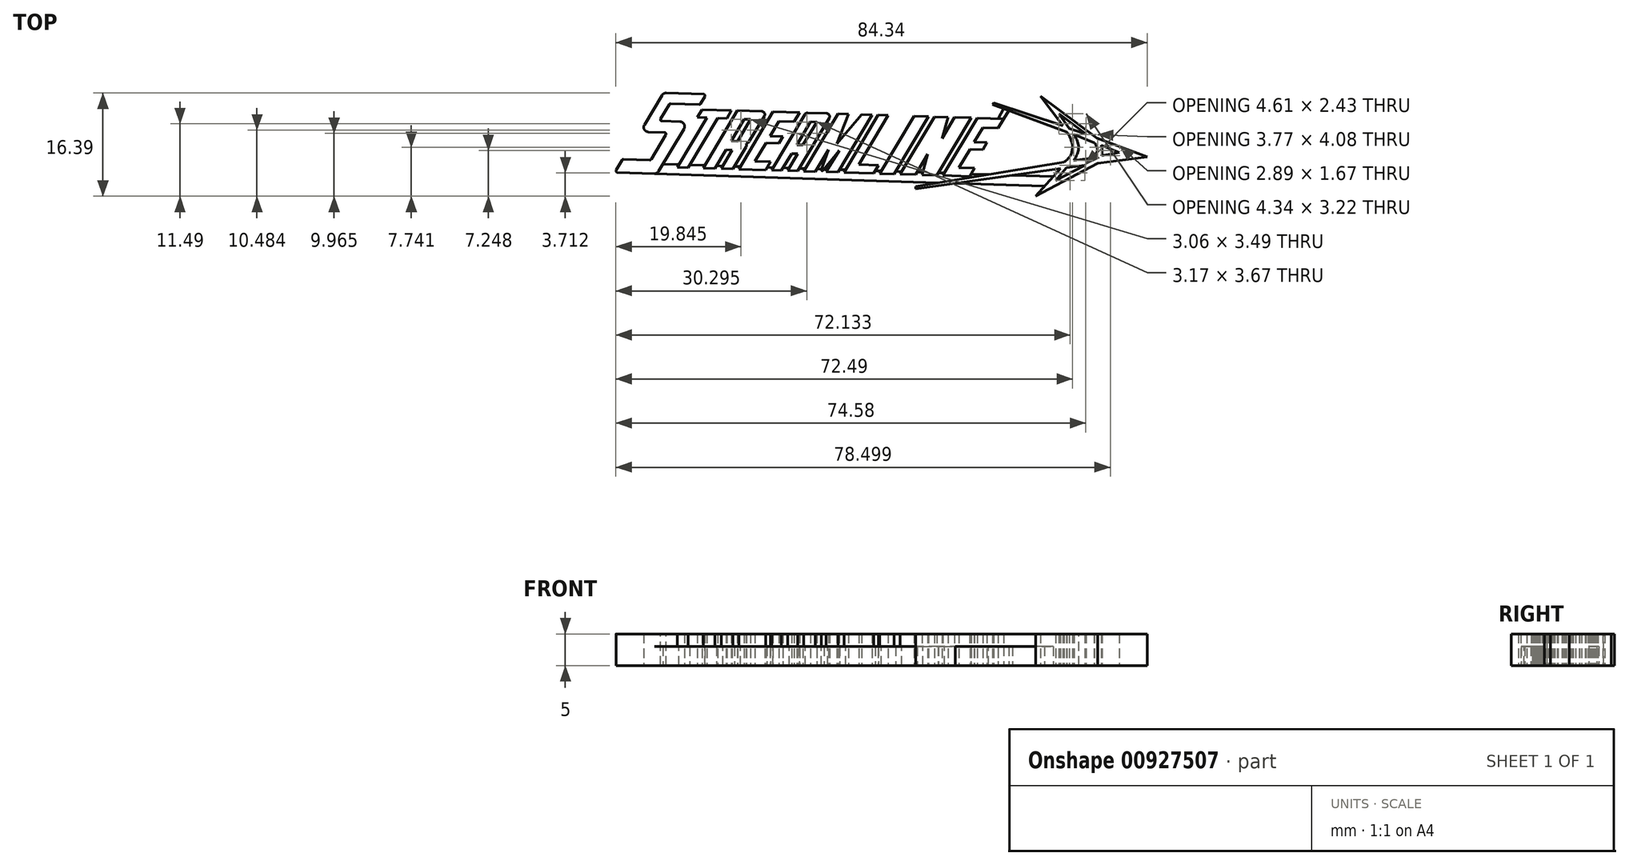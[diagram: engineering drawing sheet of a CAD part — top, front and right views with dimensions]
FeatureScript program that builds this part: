
annotation { "Feature Type Name" : "Feature", "Feature Type Description" : "" }
export const myFeature = defineFeature(function(context is Context, id is Id, definition is map)
    precondition{}
    {
        {
            var Q0;
            Q0=qCreatedBy(makeId("Top.planeOp"),FACE);
            var sketch = newSketch(context, id + "F0", { "sketchPlane" : qUnion([Q0])});
            skLineSegment(sketch, "E0", {"start": v(-39.16, -4.36) * mm, "end": v(-37.92, -2.27) * mm});
            skLineSegment(sketch, "E1", {"start": v(-37.92, -2.27) * mm, "end": v(-33.45, -2.42) * mm});
            skLineSegment(sketch, "E2", {"start": v(-33.45, -2.42) * mm, "end": v(-30.85, 1.96) * mm});
            skLineSegment(sketch, "E3", {"start": v(-30.85, 1.96) * mm, "end": v(-35.11, 2.1) * mm});
            skLineSegment(sketch, "E4", {"start": v(-35.11, 2.1) * mm, "end": v(-31.45, 8.25) * mm});
            skLineSegment(sketch, "E5", {"start": v(-31.45, 8.25) * mm, "end": v(-24.64, 8.03) * mm});
            skLineSegment(sketch, "E6", {"start": v(-24.64, 8.03) * mm, "end": v(-25.6, 6.4) * mm});
            skLineSegment(sketch, "E7", {"start": v(-25.6, 6.4) * mm, "end": v(-30.45, 6.55) * mm});
            skLineSegment(sketch, "E8", {"start": v(-30.45, 6.55) * mm, "end": v(-32.1, 3.8) * mm});
            skLineSegment(sketch, "E9", {"start": v(-32.1, 3.8) * mm, "end": v(-27.53, 3.65) * mm});
            skLineSegment(sketch, "E10", {"start": v(-27.53, 3.65) * mm, "end": v(-32.42, -4.57) * mm});
            skLineSegment(sketch, "E11", {"start": v(-32.42, -4.57) * mm, "end": v(-39.16, -4.36) * mm});
            skLineSegment(sketch, "E12", {"start": v(-29.24, -3.55) * mm, "end": v(-24.55, 4.32) * mm});
            skLineSegment(sketch, "E13", {"start": v(-24.55, 4.32) * mm, "end": v(-26.02, 4.37) * mm});
            skLineSegment(sketch, "E14", {"start": v(-26.02, 4.37) * mm, "end": v(-25.28, 5.61) * mm});
            skLineSegment(sketch, "E15", {"start": v(-25.28, 5.61) * mm, "end": v(-20.64, 5.47) * mm});
            skLineSegment(sketch, "E16", {"start": v(-20.64, 5.47) * mm, "end": v(-21.38, 4.22) * mm});
            skLineSegment(sketch, "E17", {"start": v(-21.38, 4.22) * mm, "end": v(-22.84, 4.27) * mm});
            skLineSegment(sketch, "E18", {"start": v(-22.84, 4.27) * mm, "end": v(-27.53, -3.6) * mm});
            skLineSegment(sketch, "E19", {"start": v(-27.53, -3.6) * mm, "end": v(-29.24, -3.55) * mm});
            skLineSegment(sketch, "E20", {"start": v(-25.11, -3.68) * mm, "end": v(-19.68, 5.44) * mm});
            skLineSegment(sketch, "E21", {"start": v(-19.68, 5.44) * mm, "end": v(-14.98, 5.3) * mm});
            skLineSegment(sketch, "E22", {"start": v(-14.98, 5.3) * mm, "end": v(-17.95, 0.3) * mm});
            skLineSegment(sketch, "E23", {"start": v(-17.95, 0.3) * mm, "end": v(-18.28, 0.22) * mm});
            skLineSegment(sketch, "E24", {"start": v(-18.28, 0.22) * mm, "end": v(-18.2, -0.1) * mm});
            skLineSegment(sketch, "E25", {"start": v(-18.2, -0.1) * mm, "end": v(-20.4, -3.82) * mm});
            skLineSegment(sketch, "E26", {"start": v(-20.4, -3.82) * mm, "end": v(-22.26, -3.77) * mm});
            skLineSegment(sketch, "E27", {"start": v(-22.26, -3.77) * mm, "end": v(-20.5, -0.81) * mm});
            skLineSegment(sketch, "E28", {"start": v(-20.5, -0.81) * mm, "end": v(-21.5, -0.78) * mm});
            skLineSegment(sketch, "E29", {"start": v(-21.5, -0.78) * mm, "end": v(-23.26, -3.74) * mm});
            skLineSegment(sketch, "E30", {"start": v(-23.26, -3.74) * mm, "end": v(-25.11, -3.68) * mm});
            skLineSegment(sketch, "E31", {"start": v(-20.67, 0.62) * mm, "end": v(-18.6, 4.08) * mm});
            skLineSegment(sketch, "E32", {"start": v(-18.6, 4.08) * mm, "end": v(-17.6, 4.05) * mm});
            skLineSegment(sketch, "E33", {"start": v(-17.6, 4.05) * mm, "end": v(-19.67, 0.59) * mm});
            skLineSegment(sketch, "E34", {"start": v(-19.67, 0.59) * mm, "end": v(-20.67, 0.62) * mm});
            skLineSegment(sketch, "E35", {"start": v(-19.45, -3.85) * mm, "end": v(-14.02, 5.26) * mm});
            skLineSegment(sketch, "E36", {"start": v(-14.02, 5.26) * mm, "end": v(-9.8, 5.13) * mm});
            skLineSegment(sketch, "E37", {"start": v(-9.8, 5.13) * mm, "end": v(-10.67, 3.67) * mm});
            skLineSegment(sketch, "E38", {"start": v(-10.67, 3.67) * mm, "end": v(-13.11, 3.74) * mm});
            skLineSegment(sketch, "E39", {"start": v(-13.11, 3.74) * mm, "end": v(-14.5, 1.42) * mm});
            skLineSegment(sketch, "E40", {"start": v(-14.5, 1.42) * mm, "end": v(-12.46, 1.36) * mm});
            skLineSegment(sketch, "E41", {"start": v(-12.46, 1.36) * mm, "end": v(-13.12, 0.24) * mm});
            skLineSegment(sketch, "E42", {"start": v(-13.12, 0.24) * mm, "end": v(-15.16, 0.3) * mm});
            skLineSegment(sketch, "E43", {"start": v(-15.16, 0.3) * mm, "end": v(-16.9, -2.6) * mm});
            skLineSegment(sketch, "E44", {"start": v(-16.9, -2.6) * mm, "end": v(-14.45, -2.68) * mm});
            skLineSegment(sketch, "E45", {"start": v(-14.45, -2.68) * mm, "end": v(-15.23, -3.98) * mm});
            skLineSegment(sketch, "E46", {"start": v(-15.23, -3.98) * mm, "end": v(-19.45, -3.85) * mm});
            skLineSegment(sketch, "E47", {"start": v(-14.28, -4.01) * mm, "end": v(-8.85, 5.1) * mm});
            skLineSegment(sketch, "E48", {"start": v(-8.85, 5.1) * mm, "end": v(-4.68, 4.97) * mm});
            skLineSegment(sketch, "E49", {"start": v(-4.68, 4.97) * mm, "end": v(-10.11, -4.14) * mm});
            skLineSegment(sketch, "E50", {"start": v(-10.11, -4.14) * mm, "end": v(-11.7, -4.1) * mm});
            skLineSegment(sketch, "E51", {"start": v(-11.7, -4.1) * mm, "end": v(-10.09, -1.4) * mm});
            skLineSegment(sketch, "E52", {"start": v(-10.09, -1.4) * mm, "end": v(-11.09, -1.37) * mm});
            skLineSegment(sketch, "E53", {"start": v(-11.09, -1.37) * mm, "end": v(-12.7, -4.06) * mm});
            skLineSegment(sketch, "E54", {"start": v(-12.7, -4.06) * mm, "end": v(-14.28, -4.01) * mm});
            skLineSegment(sketch, "E55", {"start": v(-9.27, -0.02) * mm, "end": v(-7.1, 3.62) * mm});
            skLineSegment(sketch, "E56", {"start": v(-7.1, 3.62) * mm, "end": v(-8.1, 3.65) * mm});
            skLineSegment(sketch, "E57", {"start": v(-8.1, 3.65) * mm, "end": v(-10.27, 0) * mm});
            skLineSegment(sketch, "E58", {"start": v(-10.27, 0) * mm, "end": v(-9.27, -0.02) * mm});
            skLineSegment(sketch, "E59", {"start": v(-9.16, -4.17) * mm, "end": v(-3.73, 4.94) * mm});
            skLineSegment(sketch, "E60", {"start": v(-3.73, 4.94) * mm, "end": v(-2.06, 4.9) * mm});
            skLineSegment(sketch, "E61", {"start": v(-2.06, 4.9) * mm, "end": v(-3.9, 0.18) * mm});
            skLineSegment(sketch, "E62", {"start": v(-3.9, 0.18) * mm, "end": v(0.04, 4.83) * mm});
            skLineSegment(sketch, "E63", {"start": v(0.04, 4.83) * mm, "end": v(1.7, 4.78) * mm});
            skLineSegment(sketch, "E64", {"start": v(1.7, 4.78) * mm, "end": v(-3.72, -4.34) * mm});
            skLineSegment(sketch, "E65", {"start": v(-3.72, -4.34) * mm, "end": v(-5.58, -4.28) * mm});
            skLineSegment(sketch, "E66", {"start": v(-5.58, -4.28) * mm, "end": v(-3.54, -0.86) * mm});
            skLineSegment(sketch, "E67", {"start": v(-3.54, -0.86) * mm, "end": v(-6.67, -4.75) * mm});
            skLineSegment(sketch, "E68", {"start": v(-6.67, -4.75) * mm, "end": v(-5.24, -0.77) * mm});
            skLineSegment(sketch, "E69", {"start": v(-5.24, -0.77) * mm, "end": v(-7.3, -4.23) * mm});
            skLineSegment(sketch, "E70", {"start": v(-7.3, -4.23) * mm, "end": v(-9.16, -4.17) * mm});
            skLineSegment(sketch, "E71", {"start": v(-2.77, -4.37) * mm, "end": v(2.66, 4.75) * mm});
            skLineSegment(sketch, "E72", {"start": v(2.66, 4.75) * mm, "end": v(4.24, 4.7) * mm});
            skLineSegment(sketch, "E73", {"start": v(4.24, 4.7) * mm, "end": v(-0.4, -3.11) * mm});
            skLineSegment(sketch, "E74", {"start": v(-0.4, -3.11) * mm, "end": v(2.74, -3.21) * mm});
            skLineSegment(sketch, "E75", {"start": v(2.74, -3.21) * mm, "end": v(1.96, -4.52) * mm});
            skLineSegment(sketch, "E76", {"start": v(1.96, -4.52) * mm, "end": v(-2.77, -4.37) * mm});
            skLineSegment(sketch, "E77", {"start": v(2.91, -4.55) * mm, "end": v(8.34, 4.57) * mm});
            skLineSegment(sketch, "E78", {"start": v(8.34, 4.57) * mm, "end": v(10.63, 4.5) * mm});
            skLineSegment(sketch, "E79", {"start": v(10.63, 4.5) * mm, "end": v(5.2, -4.62) * mm});
            skLineSegment(sketch, "E80", {"start": v(5.2, -4.62) * mm, "end": v(2.91, -4.55) * mm});
            skLineSegment(sketch, "E81", {"start": v(6.16, -4.65) * mm, "end": v(11.59, 4.47) * mm});
            skLineSegment(sketch, "E82", {"start": v(11.59, 4.47) * mm, "end": v(13.76, 4.4) * mm});
            skLineSegment(sketch, "E83", {"start": v(13.76, 4.4) * mm, "end": v(12.8, 1.04) * mm});
            skLineSegment(sketch, "E84", {"start": v(12.8, 1.04) * mm, "end": v(14.79, 4.37) * mm});
            skLineSegment(sketch, "E85", {"start": v(14.79, 4.37) * mm, "end": v(17.42, 4.29) * mm});
            skLineSegment(sketch, "E86", {"start": v(17.42, 4.29) * mm, "end": v(11.99, -4.83) * mm});
            skLineSegment(sketch, "E87", {"start": v(11.99, -4.83) * mm, "end": v(9.62, -4.75) * mm});
            skLineSegment(sketch, "E88", {"start": v(9.62, -4.75) * mm, "end": v(10.55, -1.49) * mm});
            skLineSegment(sketch, "E89", {"start": v(10.55, -1.49) * mm, "end": v(8.62, -4.72) * mm});
            skLineSegment(sketch, "E90", {"start": v(8.62, -4.72) * mm, "end": v(6.16, -4.65) * mm});
            skLineSegment(sketch, "E91", {"start": v(12.94, -4.86) * mm, "end": v(18.37, 4.26) * mm});
            skLineSegment(sketch, "E92", {"start": v(18.37, 4.26) * mm, "end": v(22.6, 4.13) * mm});
            skLineSegment(sketch, "E93", {"start": v(22.6, 4.13) * mm, "end": v(21.72, 2.66) * mm});
            skLineSegment(sketch, "E94", {"start": v(21.72, 2.66) * mm, "end": v(19.28, 2.74) * mm});
            skLineSegment(sketch, "E95", {"start": v(19.28, 2.74) * mm, "end": v(17.9, 0.42) * mm});
            skLineSegment(sketch, "E96", {"start": v(17.9, 0.42) * mm, "end": v(19.93, 0.35) * mm});
            skLineSegment(sketch, "E97", {"start": v(19.93, 0.35) * mm, "end": v(19.27, -0.76) * mm});
            skLineSegment(sketch, "E98", {"start": v(19.27, -0.76) * mm, "end": v(17.23, -0.7) * mm});
            skLineSegment(sketch, "E99", {"start": v(17.23, -0.7) * mm, "end": v(15.5, -3.6) * mm});
            skLineSegment(sketch, "E100", {"start": v(15.5, -3.6) * mm, "end": v(17.94, -3.68) * mm});
            skLineSegment(sketch, "E101", {"start": v(17.94, -3.68) * mm, "end": v(17.17, -4.99) * mm});
            skLineSegment(sketch, "E102", {"start": v(17.17, -4.99) * mm, "end": v(12.94, -4.86) * mm});
            skLineSegment(sketch, "E103", {"start": v(-17.95, 0.3) * mm, "end": v(-18.2, -0.1) * mm, "construction": true});
            skLineSegment(sketch, "E104", {"start": v(-18.07, 0.1) * mm, "end": v(-18.28, 0.22) * mm, "construction": true});
            skLineSegment(sketch, "E105", {"start": v(-27.53, -3.6) * mm, "end": v(-25.11, -3.68) * mm, "construction": true});
            skLineSegment(sketch, "E106", {"start": v(-23.26, -3.74) * mm, "end": v(-22.26, -3.77) * mm, "construction": true});
            skLineSegment(sketch, "E107", {"start": v(-20.4, -3.82) * mm, "end": v(-19.45, -3.85) * mm, "construction": true});
            skLineSegment(sketch, "E108", {"start": v(-15.23, -3.98) * mm, "end": v(-14.28, -4.01) * mm, "construction": true});
            skLineSegment(sketch, "E109", {"start": v(-12.7, -4.06) * mm, "end": v(-11.7, -4.1) * mm, "construction": true});
            skLineSegment(sketch, "E110", {"start": v(-10.11, -4.14) * mm, "end": v(-9.16, -4.17) * mm, "construction": true});
            skLineSegment(sketch, "E111", {"start": v(-7.3, -4.23) * mm, "end": v(-5.58, -4.28) * mm, "construction": true});
            skLineSegment(sketch, "E112", {"start": v(-3.72, -4.34) * mm, "end": v(-2.77, -4.37) * mm, "construction": true});
            skLineSegment(sketch, "E113", {"start": v(1.96, -4.52) * mm, "end": v(2.91, -4.55) * mm, "construction": true});
            skLineSegment(sketch, "E114", {"start": v(5.2, -4.62) * mm, "end": v(6.16, -4.65) * mm, "construction": true});
            skLineSegment(sketch, "E115", {"start": v(8.62, -4.72) * mm, "end": v(9.62, -4.75) * mm, "construction": true});
            skLineSegment(sketch, "E116", {"start": v(11.99, -4.83) * mm, "end": v(12.94, -4.86) * mm, "construction": true});
            skLineSegment(sketch, "E117", {"start": v(-20.64, 5.47) * mm, "end": v(-19.68, 5.44) * mm, "construction": true});
            skLineSegment(sketch, "E118", {"start": v(-14.98, 5.3) * mm, "end": v(-14.02, 5.26) * mm, "construction": true});
            skLineSegment(sketch, "E119", {"start": v(-9.8, 5.13) * mm, "end": v(-8.85, 5.1) * mm, "construction": true});
            skLineSegment(sketch, "E120", {"start": v(-4.68, 4.97) * mm, "end": v(-3.73, 4.94) * mm, "construction": true});
            skLineSegment(sketch, "E121", {"start": v(-2.06, 4.9) * mm, "end": v(0.04, 4.83) * mm, "construction": true});
            skLineSegment(sketch, "E122", {"start": v(1.7, 4.78) * mm, "end": v(2.66, 4.75) * mm, "construction": true});
            skLineSegment(sketch, "E123", {"start": v(4.24, 4.7) * mm, "end": v(8.34, 4.57) * mm, "construction": true});
            skLineSegment(sketch, "E124", {"start": v(10.63, 4.5) * mm, "end": v(11.59, 4.47) * mm, "construction": true});
            skLineSegment(sketch, "E125", {"start": v(13.76, 4.4) * mm, "end": v(14.79, 4.37) * mm, "construction": true});
            skLineSegment(sketch, "E126", {"start": v(17.42, 4.29) * mm, "end": v(18.37, 4.26) * mm, "construction": true});
            skLineSegment(sketch, "E127", {"start": v(-21.5, -0.78) * mm, "end": v(-20.67, 0.62) * mm, "construction": true});
            skLineSegment(sketch, "E128", {"start": v(-19.67, 0.59) * mm, "end": v(-20.5, -0.81) * mm, "construction": true});
            skLineSegment(sketch, "E129", {"start": v(-10.27, 0) * mm, "end": v(-11.09, -1.37) * mm, "construction": true});
            skLineSegment(sketch, "E130", {"start": v(-9.27, -0.02) * mm, "end": v(-10.09, -1.4) * mm, "construction": true});
            skLineSegment(sketch, "E131", {"start": v(-14.5, 1.42) * mm, "end": v(-15.16, 0.3) * mm, "construction": true});
            skLineSegment(sketch, "E132", {"start": v(17.23, -0.7) * mm, "end": v(17.9, 0.42) * mm, "construction": true});
            skLineSegment(sketch, "E133", {"start": v(-24.55, 4.32) * mm, "end": v(-22.84, 4.27) * mm, "construction": true});
            skSolve(sketch);
        }
        {
            var Q0;
            Q0=qCreatedBy(makeId("Top.planeOp"),FACE);
            var sketch = newSketch(context, id + "F1", { "sketchPlane" : qUnion([Q0])});
            skLineSegment(sketch, "E134", {"start": v(20.83, 6.41) * mm, "end": v(32.6, 2.05) * mm});
            skLineSegment(sketch, "E135", {"start": v(32.16, -2.72) * mm, "end": v(8.64, -6.59) * mm});
            skLineSegment(sketch, "E136", {"start": v(8.64, -6.59) * mm, "end": v(8.64, -6.97) * mm});
            skLineSegment(sketch, "E137", {"start": v(8.64, -6.97) * mm, "end": v(31.59, -3.75) * mm});
            skLineSegment(sketch, "E138", {"start": v(31.59, -3.75) * mm, "end": v(27.65, -8.15) * mm});
            skLineSegment(sketch, "E139", {"start": v(27.65, -8.15) * mm, "end": v(37.48, -2.9) * mm});
            skLineSegment(sketch, "E140", {"start": v(37.48, -2.9) * mm, "end": v(42.24, -2.3) * mm});
            skLineSegment(sketch, "E141", {"start": v(42.2, -0.72) * mm, "end": v(37.4, 1.06) * mm});
            skLineSegment(sketch, "E142", {"start": v(37.4, 1.06) * mm, "end": v(28.42, 7.76) * mm});
            skLineSegment(sketch, "E143", {"start": v(28.42, 7.76) * mm, "end": v(32, 3.03) * mm});
            skLineSegment(sketch, "E144", {"start": v(32, 3.03) * mm, "end": v(20.99, 6.7) * mm});
            skLineSegment(sketch, "E145", {"start": v(20.99, 6.7) * mm, "end": v(20.83, 6.41) * mm});
            skLineSegment(sketch, "E146", {"start": v(31.34, 4.95) * mm, "end": v(35.68, 1.73) * mm});
            skLineSegment(sketch, "E147", {"start": v(35.68, 1.73) * mm, "end": v(33.03, 2.63) * mm});
            skLineSegment(sketch, "E148", {"start": v(33.03, 2.63) * mm, "end": v(31.34, 4.95) * mm});
            skLineSegment(sketch, "E149", {"start": v(30.85, -5.65) * mm, "end": v(35.46, -3.22) * mm});
            skLineSegment(sketch, "E150", {"start": v(35.46, -3.22) * mm, "end": v(32.59, -3.61) * mm});
            skLineSegment(sketch, "E151", {"start": v(32.59, -3.61) * mm, "end": v(30.85, -5.65) * mm});
            skLineSegment(sketch, "E152", {"start": v(38.07, -0.06) * mm, "end": v(40.97, -1.23) * mm});
            skLineSegment(sketch, "E153", {"start": v(40.97, -1.23) * mm, "end": v(38.14, -1.74) * mm});
            skLineSegment(sketch, "E154", {"start": v(33.72, -2.45) * mm, "end": v(36.92, -2.01) * mm});
            skLineSegment(sketch, "E155", {"start": v(37.02, 0.33) * mm, "end": v(33.75, 1.63) * mm});
            skFitSpline(sketch, "E156", {"points": [v(32.6, 2.05) * mm, v(32.66, 1.96) * mm, v(32.9, 1.63) * mm, v(33.25, 0.85) * mm, v(33.52, -0.31) * mm, v(33.25, -1.56) * mm, v(32.67, -2.32) * mm, v(32.28, -2.63) * mm, v(32.16, -2.72) * mm]});
            skFitSpline(sketch, "E157", {"points": [v(38.14, -1.74) * mm, v(38.15, -1.69) * mm, v(38.18, -1.5) * mm, v(38.21, -1.18) * mm, v(38.22, -0.78) * mm, v(38.17, -0.43) * mm, v(38.12, -0.2) * mm, v(38.08, -0.1) * mm, v(38.07, -0.06) * mm]});
            skFitSpline(sketch, "E158", {"points": [v(36.92, -2.01) * mm, v(36.96, -1.94) * mm, v(37.12, -1.7) * mm, v(37.33, -1.3) * mm, v(37.49, -0.74) * mm, v(37.33, -0.24) * mm, v(37.17, 0.1) * mm, v(37.06, 0.28) * mm, v(37.02, 0.33) * mm]});
            skFitSpline(sketch, "E159", {"points": [v(33.75, 1.63) * mm, v(33.82, 1.52) * mm, v(34.02, 1.17) * mm, v(34.32, 0.48) * mm, v(34.5, -0.48) * mm, v(34.27, -1.4) * mm, v(33.98, -2.04) * mm, v(33.78, -2.35) * mm, v(33.72, -2.45) * mm]});
            skLineSegment(sketch, "E160", {"start": v(42.2, -0.72) * mm, "end": v(45.36, -1.9) * mm});
            skLineSegment(sketch, "E161", {"start": v(42.24, -2.3) * mm, "end": v(45.36, -1.9) * mm});
            skSolve(sketch);
        }
        {
            var Q0;
            Q0=qCreatedBy(makeId("Top.planeOp"),FACE);
            var sketch = newSketch(context, id + "F2", { "sketchPlane" : qUnion([Q0])});
            skLineSegment(sketch, "E162", {"start": v(-31.5, -3.03) * mm, "end": v(30.45, -5.02) * mm});
            skLineSegment(sketch, "E163", {"start": v(29.08, -6.55) * mm, "end": v(-32.42, -4.57) * mm});
            skLineSegment(sketch, "E164", {"start": v(30.45, -5.02) * mm, "end": v(29.08, -6.55) * mm});
            skLineSegment(sketch, "E165", {"start": v(22.6, 4.13) * mm, "end": v(23.39, 5.46) * mm});
            skLineSegment(sketch, "E166", {"start": v(22.61, 5.75) * mm, "end": v(21.67, 4.16) * mm});
            skLineSegment(sketch, "E167", {"start": v(21.67, 4.16) * mm, "end": v(22.6, 4.13) * mm});
            skLineSegment(sketch, "E168", {"start": v(22.61, 5.75) * mm, "end": v(23.39, 5.46) * mm});
            skLineSegment(sketch, "E169", {"start": v(-32.42, -4.57) * mm, "end": v(-31.5, -3.03) * mm});
            skSolve(sketch);
        }
        {
            var Q0;
            Q0=makeQuery(id+"F1.imprint","IMPRINT",FACE,{"disambiguationData":[TD([[makeQuery(id+"F1.imprint","IMPRINT",EDGE,{"derivedFrom":sQuery(id+"F1.wireOp",EDGE,"E134")}),1.0]])]});
            extrude(context, id + "F3", {"entities" : qUnion([Q0]), "depth" : 5 * mm, "offsetDistance" : 25 * mm});
        }
        {
            var Q0;
            Q0=makeQuery(id+"F2.imprint","IMPRINT",FACE,{"disambiguationData":[TD([[makeQuery(id+"F2.imprint","IMPRINT",EDGE,{"derivedFrom":sQuery(id+"F2.wireOp",EDGE,"E162")}),-1.0]])]});
            var Q1;
            Q1=makeQuery(id+"F2.imprint","IMPRINT",FACE,{"disambiguationData":[TD([[makeQuery(id+"F2.imprint","IMPRINT",EDGE,{"derivedFrom":sQuery(id+"F2.wireOp",EDGE,"E165")}),1.0]])]});
            extrude(context, id + "F4", {"entities" : qUnion([Q0, Q1]), "operationType" : NewBodyOperationType.ADD, "depth" : 3 * mm, "offsetDistance" : 25 * mm});
        }
        {
            var Q0;
            Q0 = qSketchRegion(id + "F0", true);
            extrude(context, id + "F5", {"entities" : qUnion([Q0]), "operationType" : NewBodyOperationType.ADD, "depth" : 5 * mm, "offsetDistance" : 25 * mm});
        }
        {
            var Q0;
            Q0=makeQuery(id+"F5.opExtrude","SWEPT_EDGE",EDGE,{"disambiguationData":[OSD([sQuery(id+"F0.wireOp",EDGE,"E67"),sQuery(id+"F0.wireOp",EDGE,"E68")])]});
            fillet(context, id + "F6", {"entities" : qUnion([Q0]), "radius" : .15 * mm, "tangentPropagation" : true, "allowEdgeOverflow" : false});
        }
        {
            var Q0;
            Q0=makeQuery(id+"F5.opExtrude","SWEPT_EDGE",EDGE,{"disambiguationData":[OSD([sQuery(id+"F0.wireOp",EDGE,"E10"),sQuery(id+"F0.wireOp",EDGE,"E11")])]});
            var Q1;
            Q1=makeQuery(id+"F5.opExtrude","SWEPT_EDGE",EDGE,{"disambiguationData":[OSD([sQuery(id+"F0.wireOp",EDGE,"E9"),sQuery(id+"F0.wireOp",EDGE,"E10")])]});
            var Q2;
            Q2=makeQuery(id+"F5.opExtrude","SWEPT_EDGE",EDGE,{"disambiguationData":[OSD([sQuery(id+"F0.wireOp",EDGE,"E3"),sQuery(id+"F0.wireOp",EDGE,"E4")])]});
            var Q3;
            Q3=makeQuery(id+"F5.opExtrude","SWEPT_EDGE",EDGE,{"disambiguationData":[OSD([sQuery(id+"F0.wireOp",EDGE,"E4"),sQuery(id+"F0.wireOp",EDGE,"E5")])]});
            fillet(context, id + "F7", {"entities" : qUnion([Q0, Q1, Q2, Q3]), "radius" : .75 * mm, "tangentPropagation" : true, "allowEdgeOverflow" : false});
        }
        {
            var Q0;
            Q0=makeQuery(id+"F5.opExtrude","SWEPT_EDGE",EDGE,{"disambiguationData":[OSD([sQuery(id+"F0.wireOp",EDGE,"E6"),sQuery(id+"F0.wireOp",EDGE,"E7")])]});
            var Q1;
            Q1=makeQuery(id+"F5.opExtrude","SWEPT_EDGE",EDGE,{"disambiguationData":[OSD([sQuery(id+"F0.wireOp",EDGE,"E5"),sQuery(id+"F0.wireOp",EDGE,"E6")])]});
            var Q2;
            Q2=makeQuery(id+"F5.opExtrude","SWEPT_EDGE",EDGE,{"disambiguationData":[OSD([sQuery(id+"F0.wireOp",EDGE,"E8"),sQuery(id+"F0.wireOp",EDGE,"E9")])]});
            var Q3;
            Q3=makeQuery(id+"F5.opExtrude","SWEPT_EDGE",EDGE,{"disambiguationData":[OSD([sQuery(id+"F0.wireOp",EDGE,"E2"),sQuery(id+"F0.wireOp",EDGE,"E3")])]});
            var Q4;
            Q4=makeQuery(id+"F5.opExtrude","SWEPT_EDGE",EDGE,{"disambiguationData":[OSD([sQuery(id+"F0.wireOp",EDGE,"E1"),sQuery(id+"F0.wireOp",EDGE,"E2")])]});
            var Q5;
            Q5=makeQuery(id+"F5.opExtrude","SWEPT_EDGE",EDGE,{"disambiguationData":[OSD([sQuery(id+"F0.wireOp",EDGE,"E0"),sQuery(id+"F0.wireOp",EDGE,"E1")])]});
            var Q6;
            Q6=makeQuery(id+"F5.opExtrude","SWEPT_EDGE",EDGE,{"disambiguationData":[OSD([sQuery(id+"F0.wireOp",EDGE,"E0"),sQuery(id+"F0.wireOp",EDGE,"E11")])]});
            var Q7;
            Q7=makeQuery(id+"F5.opExtrude","SWEPT_EDGE",EDGE,{"disambiguationData":[OSD([sQuery(id+"F0.wireOp",EDGE,"E7"),sQuery(id+"F0.wireOp",EDGE,"E8")])]});
            fillet(context, id + "F8", {"entities" : qUnion([Q0, Q1, Q2, Q3, Q4, Q5, Q6, Q7]), "radius" : .25 * mm, "tangentPropagation" : true, "allowEdgeOverflow" : false});
        }
        {
            var Q0;
            Q0=makeQuery(id+"F5.opExtrude","SWEPT_EDGE",EDGE,{"disambiguationData":[OSD([sQuery(id+"F0.wireOp",EDGE,"E21"),sQuery(id+"F0.wireOp",EDGE,"E22")])]});
            var Q1;
            Q1=makeQuery(id+"F5.opExtrude","SWEPT_EDGE",EDGE,{"disambiguationData":[OSD([sQuery(id+"F0.wireOp",EDGE,"E47"),sQuery(id+"F0.wireOp",EDGE,"E48")])]});
            var Q2;
            Q2=makeQuery(id+"F5.opExtrude","SWEPT_EDGE",EDGE,{"disambiguationData":[OSD([sQuery(id+"F0.wireOp",EDGE,"E48"),sQuery(id+"F0.wireOp",EDGE,"E49")])]});
            var Q3;
            Q3=makeQuery(id+"F5.opExtrude","SWEPT_EDGE",EDGE,{"disambiguationData":[OSD([sQuery(id+"F0.wireOp",EDGE,"E22"),sQuery(id+"F0.wireOp",EDGE,"E23")])]});
            var Q4;
            Q4=makeQuery(id+"F5.opExtrude","SWEPT_EDGE",EDGE,{"disambiguationData":[OSD([sQuery(id+"F0.wireOp",EDGE,"E24"),sQuery(id+"F0.wireOp",EDGE,"E25")])]});
            fillet(context, id + "F9", {"entities" : qUnion([Q0, Q1, Q2, Q3, Q4]), "radius" : .5 * mm, "tangentPropagation" : true, "allowEdgeOverflow" : false});
        }
    });
